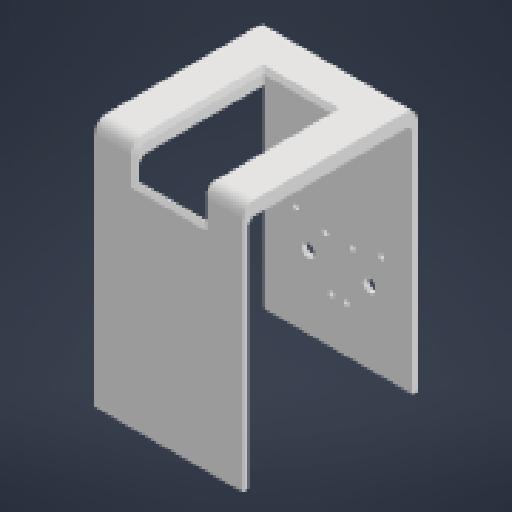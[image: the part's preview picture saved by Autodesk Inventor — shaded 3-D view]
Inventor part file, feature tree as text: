
AUTODESK INVENTOR PART (.ipt)
format: ipt  version: 2024 (Build 280153000, 153)  size: 204,288 bytes
history: native  units: in
note: dims shown in document units (in); Inventor stores cm internally (conversion verified against a paired STEP export)
features: other x6, extrude x4, sketch x4, reference x4, projected_geometry x4, fillet x2, chamfer x2
ambient origin geometry x8: Origin, YZ Plane, XZ Plane, XY Plane, X Axis, Y Axis, Z Axis, Center Point
bodies: Solid1 (feature_tree)
feature tree (26):
  extrude  "Extrusion1"  Depth=0.1575in TaperAngle=0.0deg
  extrude  "Extrusion2"  Depth=5.1181in TaperAngle=0.0deg
  extrude  "Extrusion3"  Depth=0.375in
  fillet  "Fillet1"  Radius=1.2992in
  extrude  "Extrusion5"  Depth=0.1575in TaperAngle=0.0deg
  fillet  "Fillet2"  Radius=1.4567in
  chamfer  "Chamfer1"  Distance=1.4567in
  chamfer  "Chamfer2"  Distance=4.0in
  sketch  "Sketch1"  dims[d0=7.7in d1=0.1575in d2=0.0in]
  reference  "Reference1"
  reference  "Reference2"
  reference  "Reference3"
  reference  "Reference4"
  sketch  "Sketch2"  dims[d3=0.1969in d4=5.1181in d5=0.0in]
  projected_geometry  "Projected Loop1"
  sketch  "Sketch4"  dims[d6=0.375in d7=0.2362in d8=1.2992in]
  projected_geometry  "Projected Loop3"
  projected_geometry  "Projected Loop4"
  sketch  "Sketch6"  dims[d9=1.2992in d10=0.1575in d11=0.0in d16=1.4567in d17=1.4567in d18=4.0in d19=0.0in d20=0.375in d21=0.125in d22=0.125in d23=45.0deg d24=0.1575in d25=0.125in d26=45.0deg d27=4.9213in]
  projected_geometry  "Projected Loop6"
  other  "<userpath>\Desktop\Camera_Mount.iam"
  other  "Camera_Mount.iam"
  other  "Head_Baseplate:1"
  other  "Camera_Baseplate:1"
  other  "Spur Gears:2"
  other  "Spur Gear2:1"
